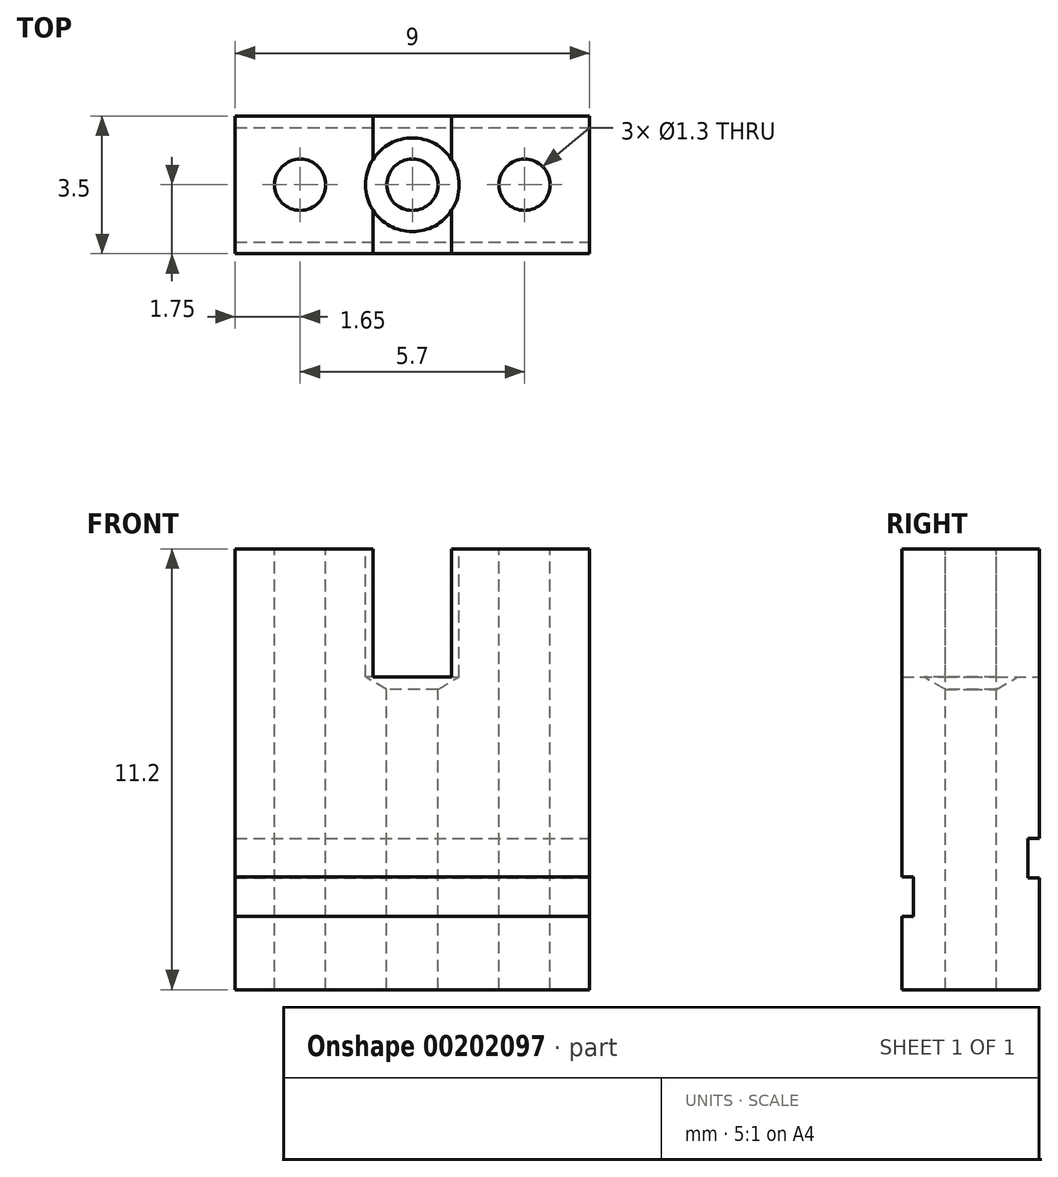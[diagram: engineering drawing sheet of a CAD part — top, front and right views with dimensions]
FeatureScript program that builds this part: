
annotation { "Feature Type Name" : "Feature", "Feature Type Description" : "" }
export const myFeature = defineFeature(function(context is Context, id is Id, definition is map)
    precondition{}
    {
        {
            var Q0;
            Q0=qCreatedBy(makeId("Top.planeOp"),FACE);
            var sketch = newSketch(context, id + "F0", { "sketchPlane" : qUnion([Q0])});
            skLineSegment(sketch, "E0.bottom", {"start": v(4.5, -1.75) * mm, "end": v(-4.5, -1.75) * mm});
            skLineSegment(sketch, "E0.top", {"start": v(4.5, 1.75) * mm, "end": v(-4.5, 1.75) * mm});
            skLineSegment(sketch, "E0.left", {"start": v(4.5, -1.75) * mm, "end": v(4.5, 1.75) * mm});
            skLineSegment(sketch, "E0.right", {"start": v(-4.5, -1.75) * mm, "end": v(-4.5, 1.75) * mm});
            skPoint(sketch, "E0.middle", {"position": v(0, 0) * mm});
            skSolve(sketch);
        }
        {
            var Q0;
            Q0 = qSketchRegion(id + "F0", true);
            extrude(context, id + "F1", {"entities" : qUnion([Q0]), "depth" : 11.2 * mm});
        }
        {
            var Q0;
            Q0=makeQuery(id+"F1.opExtrude","CAP_FACE",FACE,{"disambiguationData":[OSD([sQuery(id+"F0.wireOp",EDGE,"E0.bottom"),sQuery(id+"F0.wireOp",EDGE,"E0.top"),sQuery(id+"F0.wireOp",EDGE,"E0.left"),sQuery(id+"F0.wireOp",EDGE,"E0.right")])],"isStart":false});
            var sketch = newSketch(context, id + "F2", { "sketchPlane" : qUnion([Q0])});
            skPoint(sketch, "E1", {"position": v(0, 0) * mm});
            skPoint(sketch, "E2", {"position": v(2.85, 0) * mm});
            skPoint(sketch, "E3", {"position": v(-2.85, 0) * mm});
            skSolve(sketch);
        }
        {
            var Q0;
            Q0=sQuery(id+"F2.wireOp",VERTEX,"E1");
            var Q1;
            Q1=makeQuery(id+"F1.opExtrude","SWEPT_BODY",BODY,{"disambiguationData":[OSD([sQuery(id+"F0.wireOp",EDGE,"E0.bottom"),sQuery(id+"F0.wireOp",EDGE,"E0.top"),sQuery(id+"F0.wireOp",EDGE,"E0.left"),sQuery(id+"F0.wireOp",EDGE,"E0.right")])]});
            hole(context, id + "F3", {"style" : HoleStyle.SIMPLE, "endStyle" : HoleEndStyle.BLIND, "holeDiameter" : 2.38 * mm, "holeDepth" : 3.25 * mm, "locations" : qUnion([Q0]), "scope" : qUnion([Q1])});
        }
        {
            var Q0;
            Q0=makeQuery(id+"F1.opExtrude","CAP_FACE",FACE,{"disambiguationData":[OSD([sQuery(id+"F0.wireOp",EDGE,"E0.bottom"),sQuery(id+"F0.wireOp",EDGE,"E0.top"),sQuery(id+"F0.wireOp",EDGE,"E0.left"),sQuery(id+"F0.wireOp",EDGE,"E0.right")])],"isStart":false});
            var sketch = newSketch(context, id + "F4", { "sketchPlane" : qUnion([Q0])});
            skPoint(sketch, "E4", {"position": v(0, 0) * mm});
            skPoint(sketch, "E5", {"position": v(-2.85, 0) * mm});
            skPoint(sketch, "E6", {"position": v(2.85, 0) * mm});
            skSolve(sketch);
        }
        {
            var Q0;
            Q0=sQuery(id+"F4.wireOp",VERTEX,"E4");
            var Q1;
            Q1=sQuery(id+"F4.wireOp",VERTEX,"E5");
            var Q2;
            Q2=sQuery(id+"F4.wireOp",VERTEX,"E6");
            var Q3;
            Q3=makeQuery(id+"F1.opExtrude","SWEPT_BODY",BODY,{"disambiguationData":[OSD([sQuery(id+"F0.wireOp",EDGE,"E0.bottom"),sQuery(id+"F0.wireOp",EDGE,"E0.top"),sQuery(id+"F0.wireOp",EDGE,"E0.left"),sQuery(id+"F0.wireOp",EDGE,"E0.right")])]});
            hole(context, id + "F5", {"style" : HoleStyle.SIMPLE, "endStyle" : HoleEndStyle.THROUGH, "holeDiameter" : 1.3 * mm, "locations" : qUnion([Q0, Q1, Q2]), "scope" : qUnion([Q3]), "isTappedThrough" : true});
        }
        {
            var Q0;
            Q0=makeQuery(id+"F1.opExtrude","SWEPT_FACE",FACE,{"disambiguationData":[OSD([sQuery(id+"F0.wireOp",EDGE,"E0.bottom")])]});
            var sketch = newSketch(context, id + "F6", { "sketchPlane" : qUnion([Q0])});
            skLineSegment(sketch, "E7.bottom", {"start": v(-4.5, 2.86) * mm, "end": v(4.5, 2.86) * mm});
            skLineSegment(sketch, "E7.top", {"start": v(-4.5, 1.86) * mm, "end": v(4.5, 1.86) * mm});
            skLineSegment(sketch, "E7.left", {"start": v(-4.5, 2.86) * mm, "end": v(-4.5, 1.86) * mm});
            skLineSegment(sketch, "E7.right", {"start": v(4.5, 2.86) * mm, "end": v(4.5, 1.86) * mm});
            skPoint(sketch, "E7.middle", {"position": v(0, 2.36) * mm});
            skSolve(sketch);
        }
        {
            var Q0;
            Q0=makeQuery(id+"F6.imprint","IMPRINT",FACE,{"disambiguationData":[TD([[makeQuery(id+"F6.imprint","IMPRINT",EDGE,{"derivedFrom":sQuery(id+"F6.wireOp",EDGE,"E7.bottom")}),-1.0]])]});
            extrude(context, id + "F7", {"entities" : qUnion([Q0]), "operationType" : NewBodyOperationType.REMOVE, "oppositeDirection" : true, "depth" : 0.3 * mm});
        }
        {
            var Q0;
            Q0=makeQuery(id+"F1.opExtrude","CAP_FACE",FACE,{"disambiguationData":[OSD([sQuery(id+"F0.wireOp",EDGE,"E0.bottom"),sQuery(id+"F0.wireOp",EDGE,"E0.top"),sQuery(id+"F0.wireOp",EDGE,"E0.left"),sQuery(id+"F0.wireOp",EDGE,"E0.right")])],"isStart":false});
            var sketch = newSketch(context, id + "F8", { "sketchPlane" : qUnion([Q0])});
            skLineSegment(sketch, "E8.bottom", {"start": v(1, -1.75) * mm, "end": v(-1, -1.75) * mm});
            skLineSegment(sketch, "E8.top", {"start": v(1, 1.75) * mm, "end": v(-1, 1.75) * mm});
            skLineSegment(sketch, "E8.left", {"start": v(1, -1.75) * mm, "end": v(1, 1.75) * mm});
            skLineSegment(sketch, "E8.right", {"start": v(-1, -1.75) * mm, "end": v(-1, 1.75) * mm});
            skPoint(sketch, "E8.middle", {"position": v(0, 0) * mm});
            skSolve(sketch);
        }
        {
            var Q0;
            Q0=makeQuery(id+"F8.imprint","IMPRINT",FACE,{"disambiguationData":[TD([[makeQuery(id+"F8.imprint","IMPRINT",EDGE,{"derivedFrom":sQuery(id+"F8.wireOp",EDGE,"E8.bottom")}),-1.0]])]});
            var Q1;
            {var subQ0=sQuery(id+"F8.wireOp",EDGE,"E8.top");Q1=makeQuery(id+"F8.imprint","IMPRINT",FACE,{"disambiguationData":[TD([[makeQuery(id+"F8.imprint","IMPRINT",EDGE,{"derivedFrom":subQ0}),1.0]])]});}
            extrude(context, id + "F9", {"entities" : qUnion([Q0, Q1]), "operationType" : NewBodyOperationType.REMOVE, "oppositeDirection" : true, "depth" : 3.25 * mm});
        }
        {
            var Q0;
            Q0=makeQuery(id+"F1.opExtrude","SWEPT_FACE",FACE,{"disambiguationData":[OSD([sQuery(id+"F0.wireOp",EDGE,"E0.top")])]});
            var sketch = newSketch(context, id + "F10", { "sketchPlane" : qUnion([Q0])});
            skLineSegment(sketch, "E9.bottom", {"start": v(4.5, 2.84) * mm, "end": v(-4.5, 2.84) * mm});
            skLineSegment(sketch, "E9.top", {"start": v(4.5, 3.84) * mm, "end": v(-4.5, 3.84) * mm});
            skLineSegment(sketch, "E9.left", {"start": v(4.5, 2.84) * mm, "end": v(4.5, 3.84) * mm});
            skLineSegment(sketch, "E9.right", {"start": v(-4.5, 2.84) * mm, "end": v(-4.5, 3.84) * mm});
            skPoint(sketch, "E9.middle", {"position": v(0, 3.34) * mm});
            skSolve(sketch);
        }
        {
            var Q0;
            Q0=makeQuery(id+"F10.imprint","IMPRINT",FACE,{"disambiguationData":[TD([[makeQuery(id+"F10.imprint","IMPRINT",EDGE,{"derivedFrom":sQuery(id+"F10.wireOp",EDGE,"E9.bottom")}),-1.0]])]});
            extrude(context, id + "F11", {"entities" : qUnion([Q0]), "operationType" : NewBodyOperationType.REMOVE, "oppositeDirection" : true, "depth" : 0.3 * mm});
        }
    });
